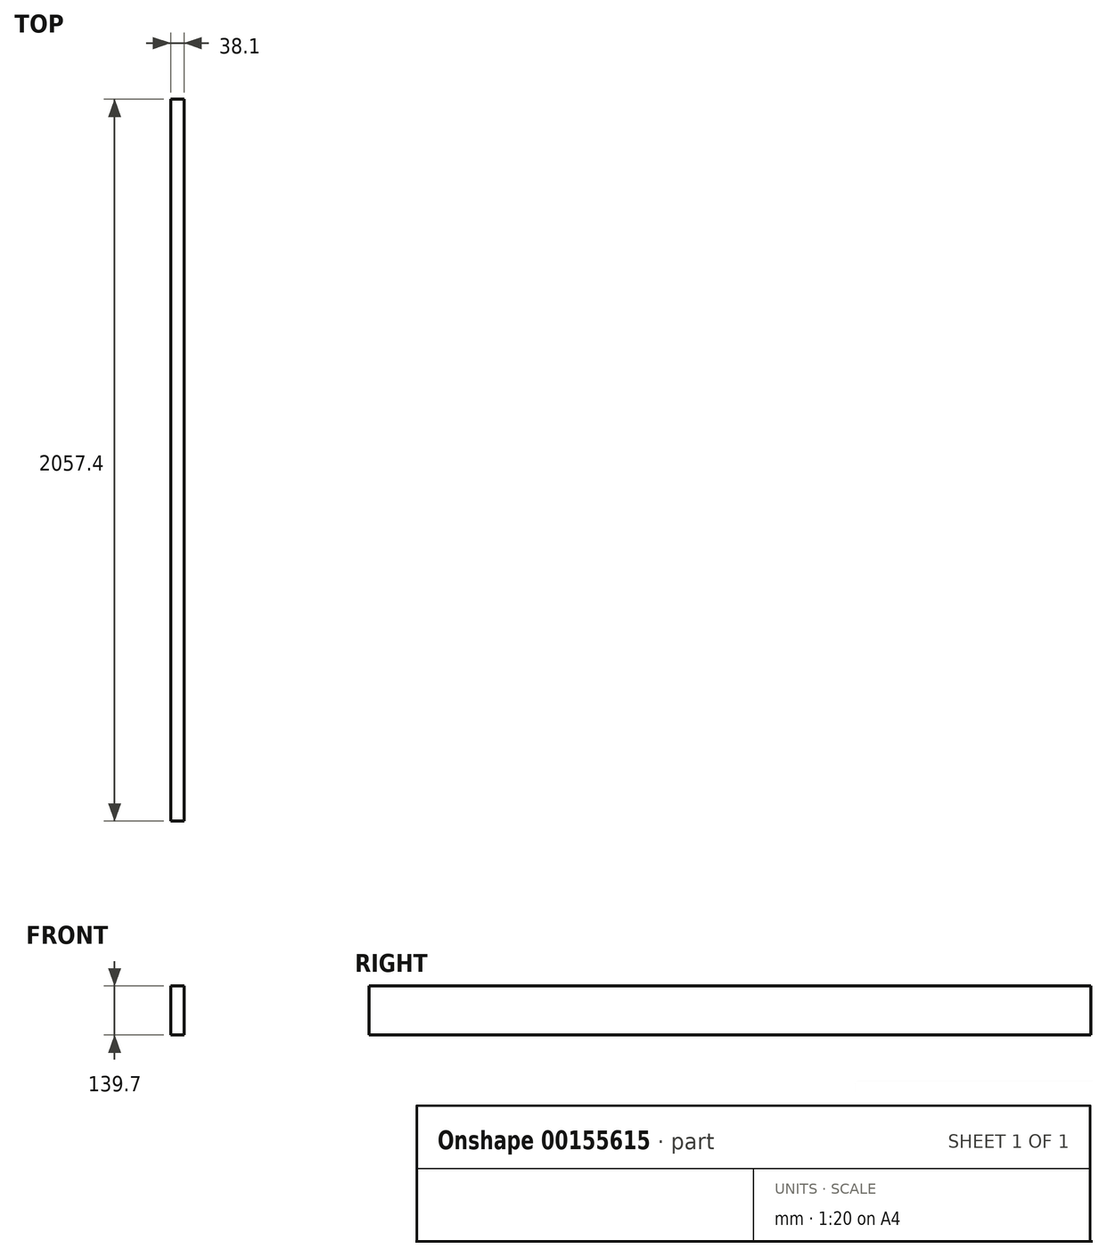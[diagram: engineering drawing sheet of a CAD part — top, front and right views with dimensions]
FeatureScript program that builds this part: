
annotation { "Feature Type Name" : "Feature", "Feature Type Description" : "" }
export const myFeature = defineFeature(function(context is Context, id is Id, definition is map)
    precondition{}
    {
        {
            var Q0;
            Q0=qCreatedBy(makeId("Front.planeOp"),FACE);
            var sketch = newSketch(context, id + "F0", { "sketchPlane" : qUnion([Q0])});
            skLineSegment(sketch, "E0.bottom", {"start": v(-19.05, 69.85) * mm, "end": v(19.05, 69.85) * mm});
            skLineSegment(sketch, "E0.top", {"start": v(-19.05, -69.85) * mm, "end": v(19.05, -69.85) * mm});
            skLineSegment(sketch, "E0.left", {"start": v(-19.05, 69.85) * mm, "end": v(-19.05, -69.85) * mm});
            skLineSegment(sketch, "E0.right", {"start": v(19.05, 69.85) * mm, "end": v(19.05, -69.85) * mm});
            skPoint(sketch, "E0.middle", {"position": v(0, 0) * mm});
            skSolve(sketch);
        }
        {
            var Q0;
            Q0=makeQuery(id+"F0.imprint","IMPRINT",FACE,{"disambiguationData":[TD([[makeQuery(id+"F0.imprint","IMPRINT",EDGE,{"derivedFrom":sQuery(id+"F0.wireOp",EDGE,"E0.bottom")}),-1.0]])]});
            extrude(context, id + "F1", {"entities" : qUnion([Q0]), "depth" : 2057.4 * mm});
        }
    });
